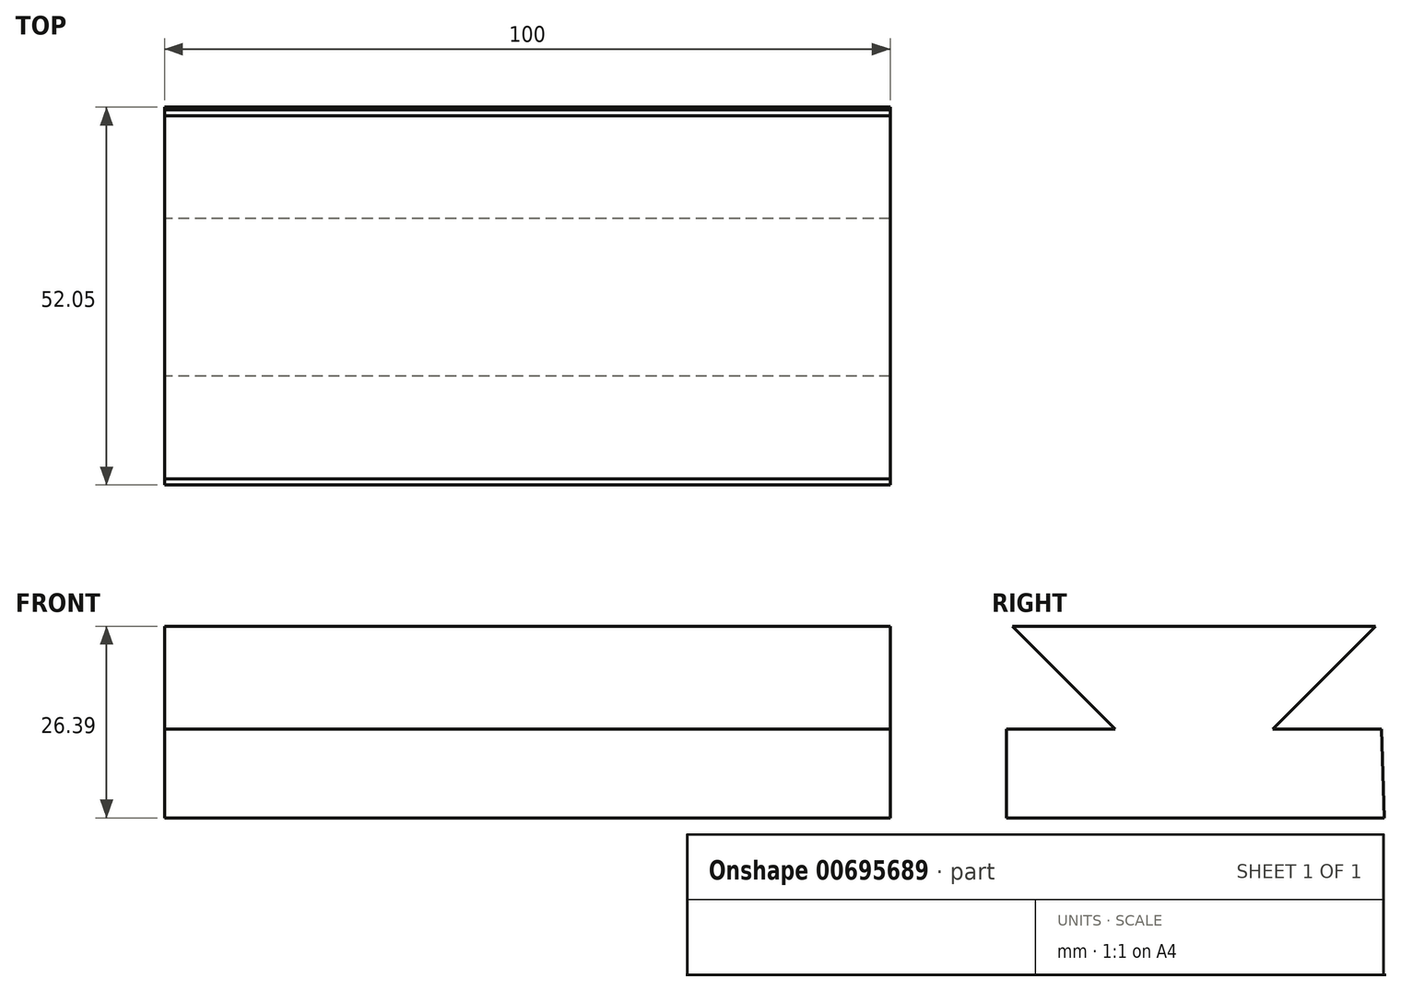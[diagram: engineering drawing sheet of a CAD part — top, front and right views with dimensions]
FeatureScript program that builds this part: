
annotation { "Feature Type Name" : "Feature", "Feature Type Description" : "" }
export const myFeature = defineFeature(function(context is Context, id is Id, definition is map)
    precondition{}
    {
        {
            var Q0;
            Q0=qCreatedBy(makeId("Right.planeOp"),FACE);
            var sketch = newSketch(context, id + "F0", { "sketchPlane" : qUnion([Q0])});
            skLineSegment(sketch, "E0", {"start": v(-46.65, 29.36) * mm, "end": v(3.35, 29.36) * mm});
            skLineSegment(sketch, "E1", {"start": v(-46.65, 29.36) * mm, "end": v(-32.5, 15.22) * mm});
            skLineSegment(sketch, "E2", {"start": v(3.35, 29.36) * mm, "end": v(-10.79, 15.22) * mm});
            skLineSegment(sketch, "E3", {"start": v(-32.5, 15.22) * mm, "end": v(-47.5, 15.22) * mm});
            skLineSegment(sketch, "E4", {"start": v(-10.79, 15.22) * mm, "end": v(4.21, 15.22) * mm});
            skLineSegment(sketch, "E5", {"start": v(-47.5, 15.22) * mm, "end": v(-47.5, 2.97) * mm});
            skLineSegment(sketch, "E6", {"start": v(-47.5, 2.97) * mm, "end": v(4.55, 2.97) * mm});
            skLineSegment(sketch, "E7", {"start": v(4.55, 2.97) * mm, "end": v(4.21, 15.22) * mm});
            skSolve(sketch);
        }
        {
            var Q0;
            Q0 = qSketchRegion(id + "F0", true);
            extrude(context, id + "F1", {"entities" : qUnion([Q0]), "depth" : 100 * mm, "offsetDistance" : 25 * mm});
        }
    });
